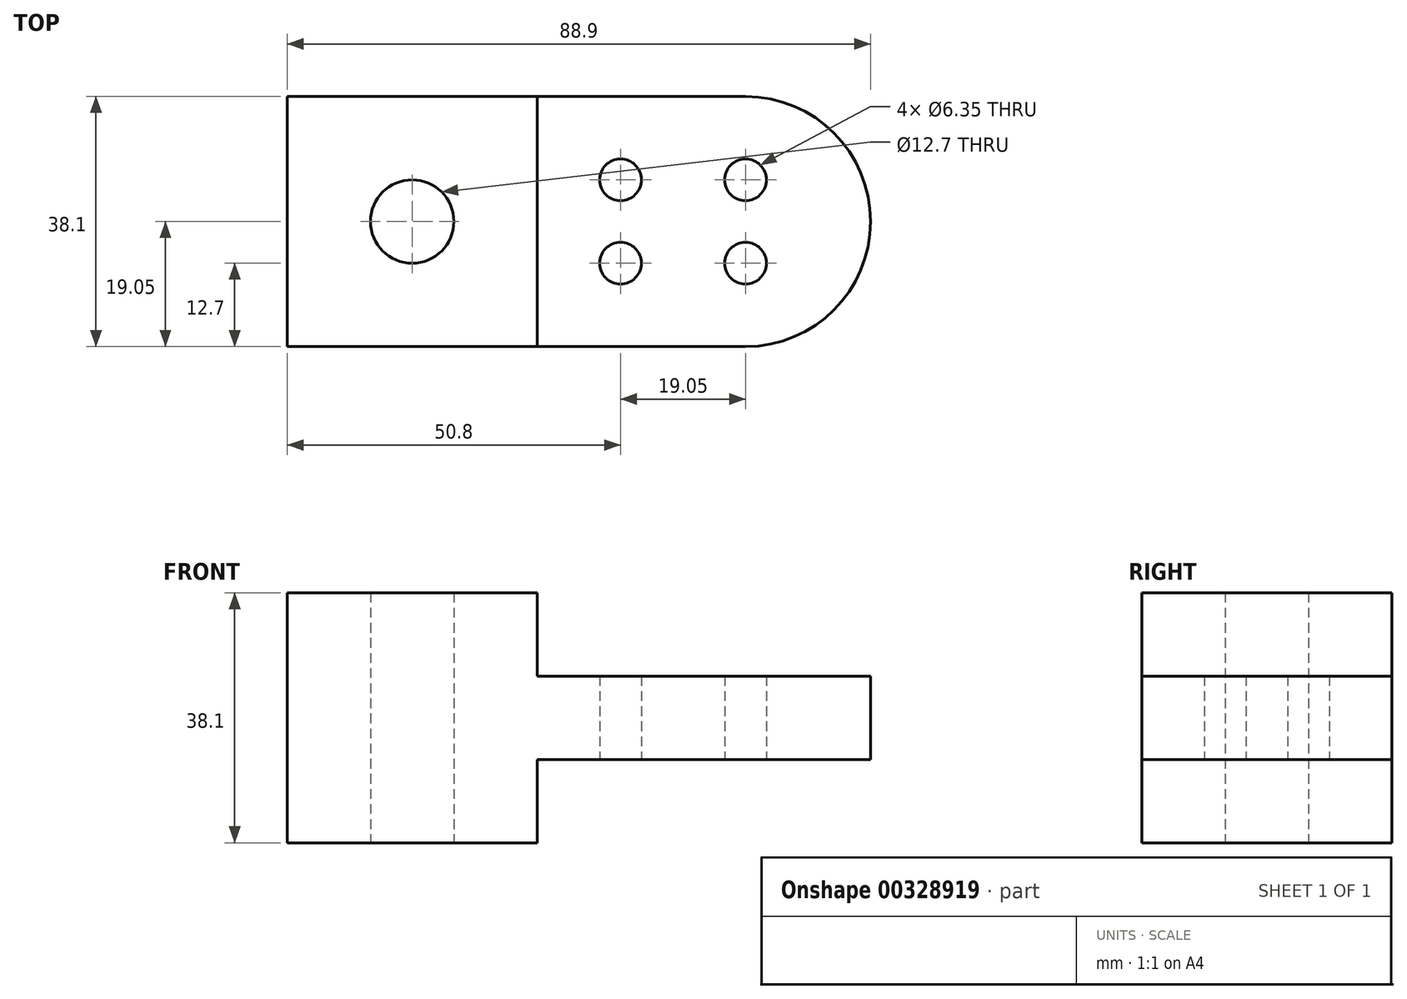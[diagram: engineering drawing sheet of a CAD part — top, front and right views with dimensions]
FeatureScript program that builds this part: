
annotation { "Feature Type Name" : "Feature", "Feature Type Description" : "" }
export const myFeature = defineFeature(function(context is Context, id is Id, definition is map)
    precondition{}
    {
        {
            var Q0;
            Q0=qCreatedBy(makeId("Top.planeOp"),FACE);
            var sketch = newSketch(context, id + "F0", { "sketchPlane" : qUnion([Q0])});
            skLineSegment(sketch, "E0.bottom", {"start": v(0, 0) * mm, "end": v(38.1, 0) * mm});
            skLineSegment(sketch, "E0.top", {"start": v(0, -38.1) * mm, "end": v(38.1, -38.1) * mm});
            skLineSegment(sketch, "E0.left", {"start": v(0, 0) * mm, "end": v(0, -38.1) * mm});
            skLineSegment(sketch, "E0.right", {"start": v(38.1, 0) * mm, "end": v(38.1, -38.1) * mm});
            skCircle(sketch, "E1", {"center": v(19.05, -19.05) * mm, "radius": 6.35 * mm});
            skPoint(sketch, "E1.centerSnap0", {"position": v(19.05, -38.1) * mm});
            skPoint(sketch, "E1.centerSnap1", {"position": v(0, -19.05) * mm});
            skLineSegment(sketch, "E2", {"start": v(38.1, 0) * mm, "end": v(69.85, 0) * mm});
            skLineSegment(sketch, "E3", {"start": v(38.1, -38.1) * mm, "end": v(69.85, -38.1) * mm});
            skPoint(sketch, "E4.startSnap0", {"position": v(38.1, -19.05) * mm});
            skArc(sketch, "E5", {"start": v(69.85, 0) * mm, "mid": v(88.9, -19.05) * mm, "end": v(69.85, -38.1) * mm});
            skLineSegment(sketch, "E6", {"start": v(38.1, 0) * mm, "end": v(50.8, 0) * mm});
            skCircle(sketch, "E7", {"center": v(50.8, -12.7) * mm, "radius": 3.18 * mm});
            skCircle(sketch, "E8", {"center": v(50.8, -25.4) * mm, "radius": 3.18 * mm});
            skCircle(sketch, "E9", {"center": v(69.85, -25.4) * mm, "radius": 3.18 * mm});
            skCircle(sketch, "E10", {"center": v(69.85, -12.7) * mm, "radius": 3.18 * mm});
            skSolve(sketch);
        }
        {
            var Q0;
            Q0=makeQuery(id+"F0.imprint","IMPRINT",FACE,{"disambiguationData":[TD([[makeQuery(id+"F0.imprint","IMPRINT",EDGE,{"derivedFrom":sQuery(id+"F0.wireOp",EDGE,"E0.bottom")}),-1.0]])]});
            var Q1;
            Q1=makeQuery(id+"F0.imprint","IMPRINT",FACE,{"disambiguationData":[TD([[makeQuery(id+"F0.imprint","IMPRINT",EDGE,{"derivedFrom":sQuery(id+"F0.wireOp",EDGE,"E0.right")}),1.0]])]});
            extrude(context, id + "F1", {"entities" : qUnion([Q0, Q1]), "depth" : 38.1 * mm});
        }
        {
            var Q0;
            Q0=makeQuery(id+"F1.opExtrude","CAP_FACE",FACE,{"disambiguationData":[OSD([sQuery(id+"F0.wireOp",EDGE,"E0.bottom"),sQuery(id+"F0.wireOp",EDGE,"E0.top"),sQuery(id+"F0.wireOp",EDGE,"E0.left"),sQuery(id+"F0.wireOp",EDGE,"E1"),sQuery(id+"F0.wireOp",EDGE,"E2"),sQuery(id+"F0.wireOp",EDGE,"E3"),sQuery(id+"F0.wireOp",EDGE,"E5"),sQuery(id+"F0.wireOp",EDGE,"E6"),sQuery(id+"F0.wireOp",EDGE,"E7"),sQuery(id+"F0.wireOp",EDGE,"E8"),sQuery(id+"F0.wireOp",EDGE,"E9"),sQuery(id+"F0.wireOp",EDGE,"E10")])],"isStart":false});
            var sketch = newSketch(context, id + "F2", { "sketchPlane" : qUnion([Q0])});
            skLineSegment(sketch, "E11", {"start": v(38.1, 0) * mm, "end": v(69.85, 0) * mm});
            skLineSegment(sketch, "E12", {"start": v(38.1, -38.1) * mm, "end": v(69.85, -38.1) * mm});
            skLineSegment(sketch, "E13", {"start": v(38.1, 0) * mm, "end": v(38.1, -38.1) * mm});
            skArc(sketch, "E14", {"start": v(69.85, 0) * mm, "mid": v(88.9, -19.05) * mm, "end": v(69.85, -38.1) * mm});
            skSolve(sketch);
        }
        {
            var Q0;
            Q0=makeQuery(id+"F2.imprint","IMPRINT",FACE,{"disambiguationData":[TD([[makeQuery(id+"F2.imprint","IMPRINT",EDGE,{"derivedFrom":sQuery(id+"F2.wireOp",EDGE,"E11")}),-1.0]])]});
            extrude(context, id + "F3", {"entities" : qUnion([Q0]), "operationType" : NewBodyOperationType.REMOVE, "oppositeDirection" : true, "depth" : 12.7 * mm});
        }
        {
            var Q0;
            Q0=makeQuery(id+"F1.opExtrude","CAP_FACE",FACE,{"disambiguationData":[OSD([sQuery(id+"F0.wireOp",EDGE,"E0.bottom"),sQuery(id+"F0.wireOp",EDGE,"E0.top"),sQuery(id+"F0.wireOp",EDGE,"E0.left"),sQuery(id+"F0.wireOp",EDGE,"E1"),sQuery(id+"F0.wireOp",EDGE,"E2"),sQuery(id+"F0.wireOp",EDGE,"E3"),sQuery(id+"F0.wireOp",EDGE,"E5"),sQuery(id+"F0.wireOp",EDGE,"E6"),sQuery(id+"F0.wireOp",EDGE,"E7"),sQuery(id+"F0.wireOp",EDGE,"E8"),sQuery(id+"F0.wireOp",EDGE,"E9"),sQuery(id+"F0.wireOp",EDGE,"E10")])],"isStart":true});
            var sketch = newSketch(context, id + "F4", { "sketchPlane" : qUnion([Q0])});
            skLineSegment(sketch, "E15", {"start": v(38.1, 38.1) * mm, "end": v(69.85, 38.1) * mm});
            skLineSegment(sketch, "E16", {"start": v(38.1, 0) * mm, "end": v(69.85, 0) * mm});
            skLineSegment(sketch, "E17", {"start": v(38.1, 38.1) * mm, "end": v(38.1, 0) * mm});
            skArc(sketch, "E18", {"start": v(69.85, 38.1) * mm, "mid": v(88.9, 19.05) * mm, "end": v(69.85, 0) * mm});
            skSolve(sketch);
        }
        {
            var Q0;
            Q0=makeQuery(id+"F4.imprint","IMPRINT",FACE,{"disambiguationData":[TD([[makeQuery(id+"F4.imprint","IMPRINT",EDGE,{"derivedFrom":sQuery(id+"F4.wireOp",EDGE,"E15")}),-1.0]])]});
            extrude(context, id + "F5", {"entities" : qUnion([Q0]), "operationType" : NewBodyOperationType.REMOVE, "oppositeDirection" : true, "depth" : 12.7 * mm});
        }
    });
